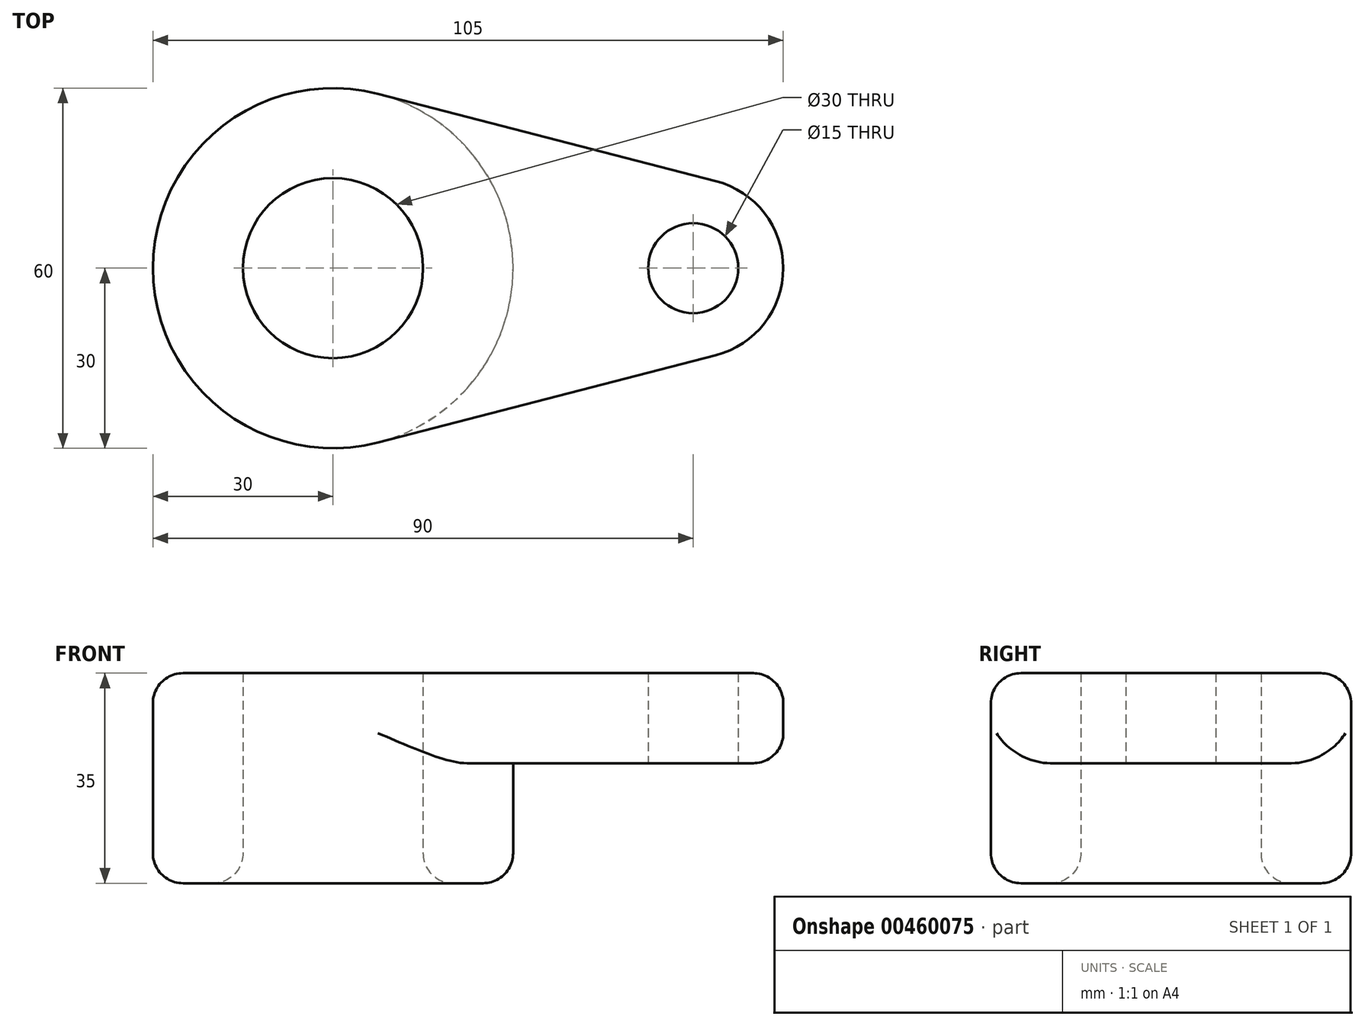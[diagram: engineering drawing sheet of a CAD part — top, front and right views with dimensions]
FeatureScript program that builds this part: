
annotation { "Feature Type Name" : "Feature", "Feature Type Description" : "" }
export const myFeature = defineFeature(function(context is Context, id is Id, definition is map)
    precondition{}
    {
        {
            var Q0;
            Q0=qCreatedBy(makeId("Top.planeOp"),FACE);
            var sketch = newSketch(context, id + "F0", { "sketchPlane" : qUnion([Q0])});
            skCircle(sketch, "E0", {"center": v(0, 0) * mm, "radius": 30 * mm});
            skCircle(sketch, "E1", {"center": v(60, 0) * mm, "radius": 15 * mm});
            skLineSegment(sketch, "E2", {"start": v(7.5, 29.05) * mm, "end": v(63.75, 14.52) * mm});
            skLineSegment(sketch, "E3", {"start": v(7.5, -29.05) * mm, "end": v(63.75, -14.52) * mm});
            skCircle(sketch, "E4", {"center": v(0, 0) * mm, "radius": 15 * mm});
            skCircle(sketch, "E5", {"center": v(60, 0) * mm, "radius": 7.5 * mm});
            skSolve(sketch);
        }
        {
            var Q0;
            Q0=makeQuery(id+"F0.imprint","IMPRINT",FACE,{"disambiguationData":[TD([[makeQuery(id+"F0.imprint","IMPRINT",EDGE,{"derivedFrom":sQuery(id+"F0.wireOp",EDGE,"E4")}),-1.0]])]});
            var Q1;
            {var subQ0=sQuery(id+"F0.wireOp",EDGE,"E2");Q1=makeQuery(id+"F0.imprint","IMPRINT",FACE,{"disambiguationData":[TD([[makeQuery(id+"F0.imprint","IMPRINT",EDGE,{"derivedFrom":subQ0}),-1.0]])]});}
            var Q2;
            Q2=makeQuery(id+"F0.imprint","IMPRINT",FACE,{"disambiguationData":[TD([[makeQuery(id+"F0.imprint","IMPRINT",EDGE,{"derivedFrom":sQuery(id+"F0.wireOp",EDGE,"E5")}),-1.0]])]});
            extrude(context, id + "F1", {"entities" : qUnion([Q0, Q1, Q2]), "depth" : 15 * mm});
        }
        {
            var Q0;
            Q0=makeQuery(id+"F0.imprint","IMPRINT",FACE,{"disambiguationData":[TD([[makeQuery(id+"F0.imprint","IMPRINT",EDGE,{"derivedFrom":sQuery(id+"F0.wireOp",EDGE,"E4")}),-1.0]])]});
            extrude(context, id + "F2", {"entities" : qUnion([Q0]), "operationType" : NewBodyOperationType.ADD, "oppositeDirection" : true, "depth" : 20 * mm});
        }
        {
            var Q0;
            Q0=makeQuery(id+"F2.opExtrude","CAP_FACE",FACE,{"disambiguationData":[OSD([sQuery(id+"F0.wireOp",EDGE,"E0"),sQuery(id+"F0.wireOp",EDGE,"E4")])],"isStart":false});
            fillet(context, id + "F3", {"entities" : qUnion([Q0]), "radius" : 5 * mm, "tangentPropagation" : true, "allowEdgeOverflow" : false});
        }
        {
            var Q0;
            Q0=makeQuery(id+"F1.opExtrude","SWEPT_FACE",FACE,{"disambiguationData":[OSD([sQuery(id+"F0.wireOp",EDGE,"E3")])]});
            var Q1;
            Q1=makeQuery(id+"F1.opExtrude","SWEPT_FACE",FACE,{"disambiguationData":[OSD([sQuery(id+"F0.wireOp",EDGE,"E1")])]});
            var Q2;
            Q2=makeQuery(id+"F1.opExtrude","SWEPT_FACE",FACE,{"disambiguationData":[OSD([sQuery(id+"F0.wireOp",EDGE,"E2")])]});
            fillet(context, id + "F4", {"entities" : qUnion([Q0, Q1, Q2]), "radius" : 5 * mm, "tangentPropagation" : true, "allowEdgeOverflow" : false});
        }
    });
